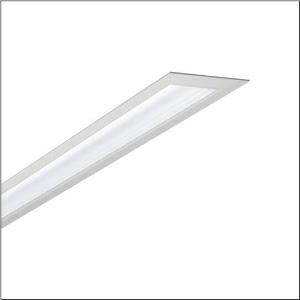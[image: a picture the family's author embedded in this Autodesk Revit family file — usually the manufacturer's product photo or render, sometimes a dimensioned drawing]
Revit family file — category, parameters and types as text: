
# Revit family: silica_r_5mx11dd1w4a_74f3
name_source: partatom
category: Lighting Fixtures
units: mm (PartAtom-declared; Revit-internal decimal feet)

## family parameters
Cut with Voids When Loaded = No
Host = Face
Light Source = No
Part Type = Normal
Room Calculation Point = No
Round Connector Dimension = Use Diameter
Shared = No

## types (1)
- --- (1 x LED, 3140 lm, 22.6 W, 4000K)
    Apparent Load = 23 VA
    CIE Flux Codes = 47 79 96 100 100
    Color Rendering = 80
    Color Temperature = 4000K
    Default Elevation = 1800 mm
    Description = Silica®, office luminaire, of aluminium, opal, light emission: direct distribution, primary light characteristic: symmetric, installation type: recessed, LED, rated luminous flux: 3.010lm, luminous efficacy: 123lm/W, light colour: 840, colour temperature: 4000K, control gear: ECG DALI, with terminal, 3+2-pole, max. 2.5mm², mains connection: 230V, AC, 50/60Hz, rated input power: 24W, luminaire housing, of aluminium, matt pure white (RAL 9010), length: 1.462mm, width: 93mm, height: 60mm, end cap, of diecast zinc, pure white (RAL 9010), protection rating (complete): IP20, insulation class (complete): insulation class I (protective earthing), certification: CE, permissible operating ambient temperature: 0..+35°C, standard: EN 50419, packaging unit: 1 piece
    Height = 0 mm  [stored 0 ft]
    Lamp = 1 x LED
    Lamp Light Flux = 3140 lm
    Lamp Power = 22.6 W
    Lamp count = 1
    Length = 1462 mm
    Luminous efficacy = 139 lm/W
    Manufacturer = Siteco
    ModVariant = No
    Model = 5MX11DD1W4A
    Mounting Place = Ceiling
    Mounting Type = Recessed
    Number of Poles = 1
    OnlyDefault = Yes
    Power Factor = 1
    Product Name = Silica®
    Product group = office luminaire | ceiling recessed
    ProductGroupID = 401
    Protection Class = Protection class I
    Protection Degree = IP 20
    RLX_Detail_Level = 1
    RLX_Emergency_Light_Flux = 0 lm
    RLX_Emergency_Type = 0
    RLX_Emergency_Type_DB = No
    RlxData = <blob elided: 23909 chars, md5=4650c0f7>
    Socket = socket
    Standby Power = 0 W
    System Light Flux = 3140 lm
    System Power = 23 W
    Type Comments = factory setting: luminous flux: 100 % | dim-lin: 254 | 125 mA
    Type Image = l_1004825.jpg
    URL = http://relux.com
    VarID = @adj_152831
    Voltage = 0 V
    Weight = 0.00 kg
    Width = 93 mm

note: [stored X ft] marks values corroborated as IEEE doubles in the binary element streams (Revit-internal decimal feet)

## geometry (parser evidence)
native form markers: Blend x4, Sweep x10
no freeform markers — native parametric forms only
